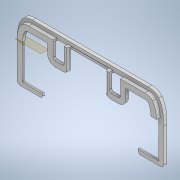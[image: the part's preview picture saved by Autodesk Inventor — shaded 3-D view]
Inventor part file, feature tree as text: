
AUTODESK INVENTOR PART (.ipt)
format: ipt  version: 2022 (Build 260153000, 153)  size: 806,912 bytes
history: native  units: mm
features: other x11, reference x7, extrude x5, sketch x5, fillet x3, projected_geometry x3, chamfer x1
ambient origin geometry x8: Origin, YZ Plane, XZ Plane, XY Plane, X Axis, Y Axis, Z Axis, Center Point
bodies: Body1 (feature_tree)
feature tree (35):
  other  "Твердое тело1"
  extrude  "Выдавливание1"  Depth=5.0mm
  sketch  "Эскиз2"
  other  "РабПлоскость1"
  other  "РабПлоскость2"
  other  "РабПлоскость3"
  extrude  "Выдавливание2"  Depth=5.0mm
  extrude  "Выдавливание3"  Depth=5.0mm
  extrude  "Выдавливание4"  Depth=0.2mm
  chamfer  "Фаска1"  Distance=0.2mm
  other  "РабПлоскость4"
  fillet  "Сопряжение1"  Radius=0.2mm
  fillet  "Сопряжение5"  Radius=5.0mm
  sketch  "Эскиз8"
  other  "РабПлоскость6"
  extrude  "Выдавливание6"  Depth=3.0mm TaperAngle=0.0deg
  fillet  "Сопряжение6"  Radius=3.3mm
  sketch  "Эскиз1"
  reference  "Ссылка2"
  reference  "Ссылка3"
  reference  "Ссылка4"
  reference  "Ссылка5"
  sketch  "Эскиз3"
  projected_geometry  "Спроецированная петля1"
  sketch  "Эскиз4"
  projected_geometry  "Спроецированная петля2"
  reference  "Ссылка8"
  reference  "Ссылка9"
  projected_geometry  "Спроецированная петля7"
  reference  "Ссылка11"
  other  "<userpath>\Documents\Git\MZCAT_2024_construction\MZCAT_2024_RPI_2\MZCAT_4.iam"
  other  "MZCAT_4.iam"
  other  "commutationCATboard:1"
  other  "motherboard_plate:1"
  other  "<userpath>\Documents\Git\MZCAT_2024\MZCAT_4.iam"
